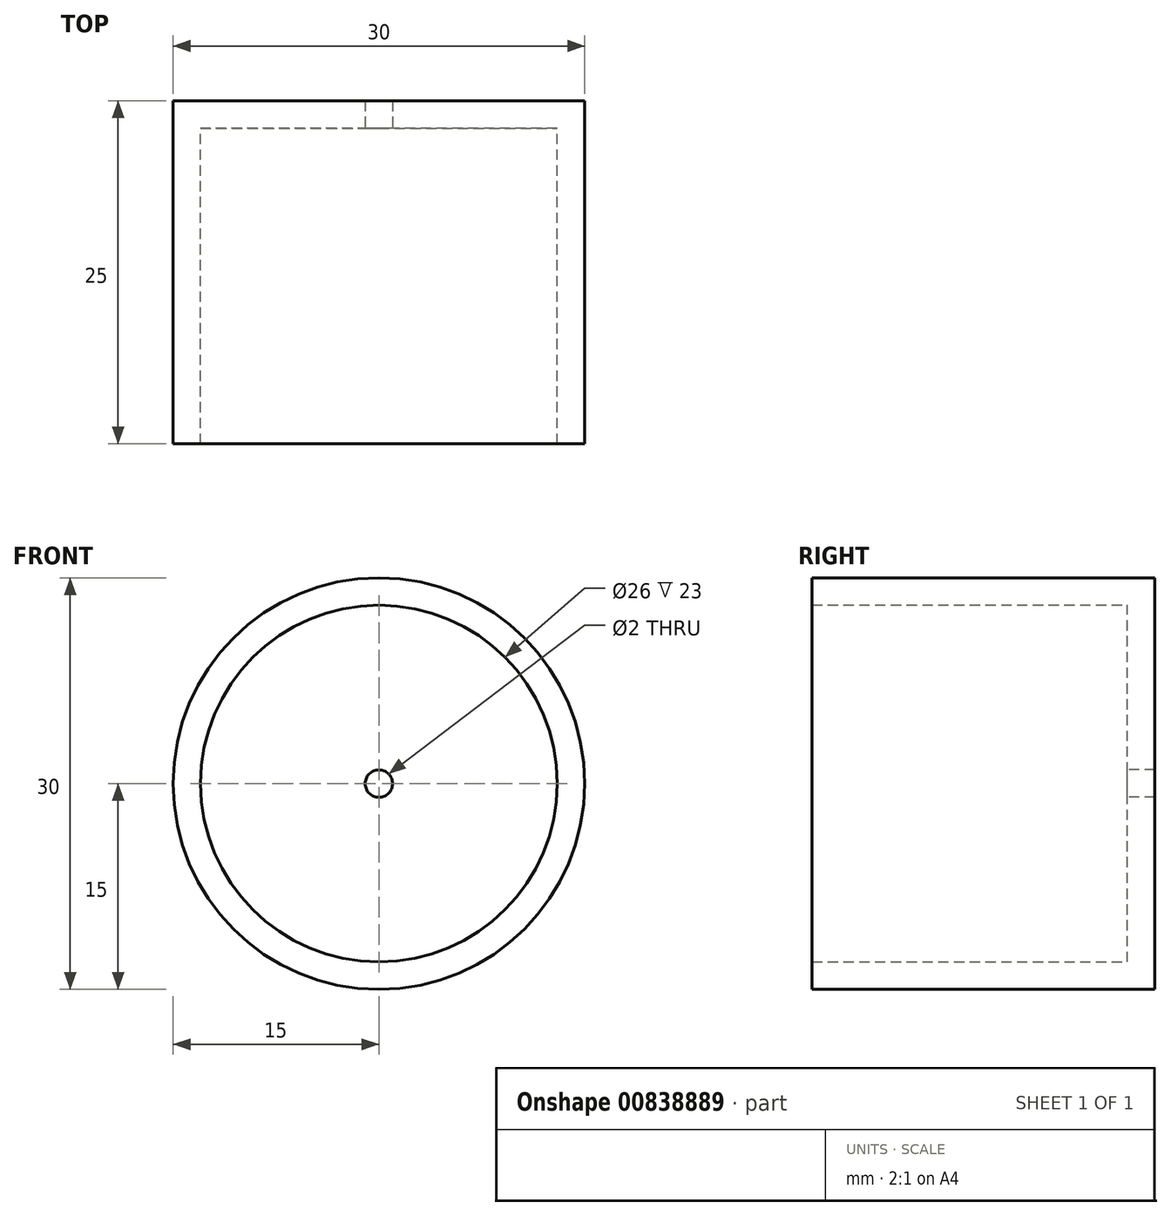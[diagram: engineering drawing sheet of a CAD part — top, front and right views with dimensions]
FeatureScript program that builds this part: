
annotation { "Feature Type Name" : "Feature", "Feature Type Description" : "" }
export const myFeature = defineFeature(function(context is Context, id is Id, definition is map)
    precondition{}
    {
        {
            var Q0;
            Q0=qCreatedBy(makeId("Front.planeOp"),FACE);
            var sketch = newSketch(context, id + "F0", { "sketchPlane" : qUnion([Q0])});
            skCircle(sketch, "E0", {"center": v(0, 0) * mm, "radius": 15 * mm});
            skSolve(sketch);
        }
        {
            var Q0;
            Q0=makeQuery(id+"F0.imprint","IMPRINT",FACE,{"disambiguationData":[TD([[makeQuery(id+"F0.imprint","IMPRINT",EDGE,{"derivedFrom":sQuery(id+"F0.wireOp",EDGE,"E0")}),1.0]])]});
            extrude(context, id + "F1", {"entities" : qUnion([Q0]), "depth" : 25 * mm, "offsetDistance" : 25 * mm});
        }
        {
            var Q0;
            Q0=makeQuery(id+"F1.opExtrude","CAP_FACE",FACE,{"disambiguationData":[OSD([sQuery(id+"F0.wireOp",EDGE,"E0")])],"isStart":false});
            var sketch = newSketch(context, id + "F2", { "sketchPlane" : qUnion([Q0])});
            skCircle(sketch, "E1", {"center": v(0, 0) * mm, "radius": 12.55 * mm});
            skSolve(sketch);
        }
        {
            var Q0;
            Q0=sQuery(id+"F2.wireOp",VERTEX,"E1.center");
            var Q1;
            Q1=makeQuery(id+"F1.opExtrude","SWEPT_BODY",BODY,{"disambiguationData":[OSD([sQuery(id+"F0.wireOp",EDGE,"E0")])]});
            hole(context, id + "F3", {"style" : HoleStyle.SIMPLE, "endStyle" : HoleEndStyle.BLIND, "holeDiameter" : 25.1 * mm, "majorDiameter" : 5 * mm, "holeDepth" : 20 * mm, "isTappedThrough" : true, "tappedDepth" : 12 * mm, "tapClearance" : 3, "locations" : qUnion([Q0]), "scope" : qUnion([Q1])});
        }
        {
            var Q0;
            Q0=makeQuery(id+"F1.opExtrude","SWEPT_BODY",BODY,{"disambiguationData":[OSD([sQuery(id+"F0.wireOp",EDGE,"E0")])]});
            deleteBodies(context, id + "F4", {"entities" : qUnion([Q0])});
        }
        {
            var Q0;
            Q0=qCreatedBy(makeId("Front.planeOp"),FACE);
            var sketch = newSketch(context, id + "F5", { "sketchPlane" : qUnion([Q0])});
            skCircle(sketch, "E2", {"center": v(0, 0) * mm, "radius": 15 * mm});
            skSolve(sketch);
        }
        {
            var Q0;
            Q0=makeQuery(id+"F5.imprint","IMPRINT",FACE,{"disambiguationData":[TD([[makeQuery(id+"F5.imprint","IMPRINT",EDGE,{"derivedFrom":sQuery(id+"F5.wireOp",EDGE,"E2")}),1.0]])]});
            extrude(context, id + "F6", {"entities" : qUnion([Q0]), "depth" : 25 * mm, "offsetDistance" : 25 * mm});
        }
        {
            var Q0;
            Q0=makeQuery(id+"F6.opExtrude","CAP_FACE",FACE,{"disambiguationData":[OSD([sQuery(id+"F5.wireOp",EDGE,"E2")])],"isStart":false});
            var sketch = newSketch(context, id + "F7", { "sketchPlane" : qUnion([Q0])});
            skCircle(sketch, "E3", {"center": v(0, 0) * mm, "radius": 14 * mm});
            skSolve(sketch);
        }
        {
            var Q0;
            Q0=makeQuery(id+"F6.opExtrude","CAP_FACE",FACE,{"disambiguationData":[OSD([sQuery(id+"F5.wireOp",EDGE,"E2")])],"isStart":false});
            shell(context, id + "F8", {"entities" : qUnion([Q0]), "thickness" : 2 * mm});
        }
        {
            var Q0;
            Q0=sQuery(id+"F7.wireOp",VERTEX,"E3.center");
            var Q1;
            Q1=makeQuery(id+"F6.opExtrude","SWEPT_BODY",BODY,{"disambiguationData":[OSD([sQuery(id+"F5.wireOp",EDGE,"E2")])]});
            hole(context, id + "F9", {"style" : HoleStyle.SIMPLE, "endStyle" : HoleEndStyle.THROUGH, "holeDiameter" : 2 * mm, "majorDiameter" : 5 * mm, "isTappedThrough" : true, "tappedDepth" : 12 * mm, "tapClearance" : 3, "locations" : qUnion([Q0]), "scope" : qUnion([Q1])});
        }
    });
